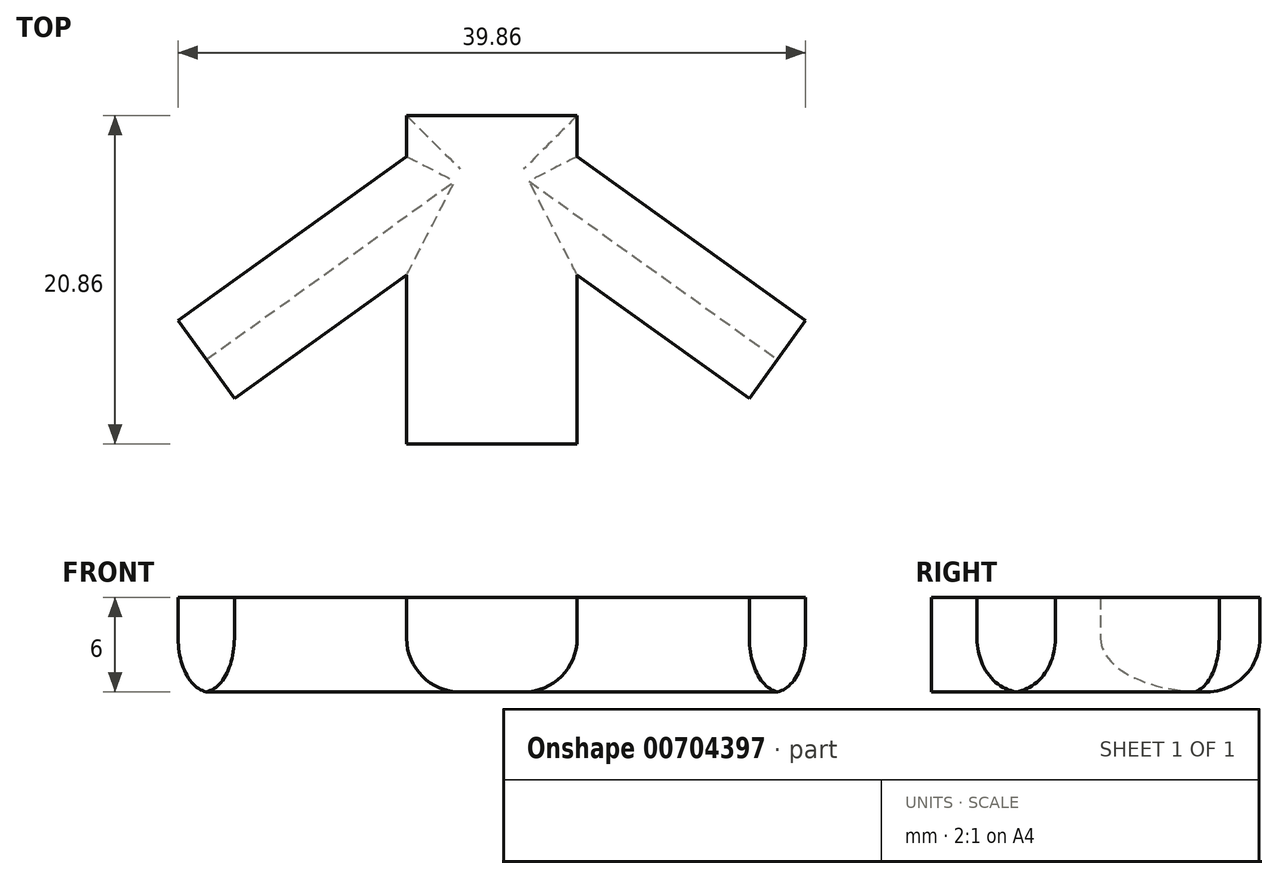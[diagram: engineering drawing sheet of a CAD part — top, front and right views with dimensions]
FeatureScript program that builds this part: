
annotation { "Feature Type Name" : "Feature", "Feature Type Description" : "" }
export const myFeature = defineFeature(function(context is Context, id is Id, definition is map)
    precondition{}
    {
        {
            var Q0;
            Q0=qCreatedBy(makeId("Top.planeOp"),FACE);
            var sketch = newSketch(context, id + "F0", { "sketchPlane" : qUnion([Q0])});
            skLineSegment(sketch, "E0", {"start": v(-5.41, 0) * mm, "end": v(-5.41, -10.73) * mm});
            skLineSegment(sketch, "E1", {"start": v(-5.41, -10.73) * mm, "end": v(0, -10.73) * mm});
            skLineSegment(sketch, "E2", {"start": v(-5.41, 0) * mm, "end": v(-16.36, -7.85) * mm});
            skLineSegment(sketch, "E3", {"start": v(-16.36, -7.85) * mm, "end": v(-19.93, -2.87) * mm});
            skLineSegment(sketch, "E4", {"start": v(-19.93, -2.87) * mm, "end": v(-5.41, 7.54) * mm});
            skLineSegment(sketch, "E5", {"start": v(-5.41, 7.54) * mm, "end": v(0, 7.54) * mm});
            skLineSegment(sketch, "E6.MirrorCS", {"start": v(5.41, -10.73) * mm, "end": v(0, -10.73) * mm});
            skLineSegment(sketch, "E7.MirrorCS", {"start": v(5.41, 0) * mm, "end": v(5.41, -10.73) * mm});
            skLineSegment(sketch, "E8.MirrorCS", {"start": v(5.41, 0) * mm, "end": v(16.36, -7.85) * mm});
            skLineSegment(sketch, "E9.MirrorCS", {"start": v(16.36, -7.85) * mm, "end": v(19.93, -2.87) * mm});
            skLineSegment(sketch, "E10.MirrorCS", {"start": v(19.93, -2.87) * mm, "end": v(5.41, 7.54) * mm});
            skLineSegment(sketch, "E11.MirrorCS", {"start": v(5.41, 7.54) * mm, "end": v(0, 7.54) * mm});
            skLineSegment(sketch, "E12", {"start": v(-5.41, 7.54) * mm, "end": v(-5.41, 10.13) * mm});
            skLineSegment(sketch, "E13", {"start": v(-5.41, 10.13) * mm, "end": v(0, 10.13) * mm});
            skLineSegment(sketch, "E14.MirrorCS", {"start": v(5.41, 10.13) * mm, "end": v(0, 10.13) * mm});
            skLineSegment(sketch, "E15.MirrorCS", {"start": v(5.41, 7.54) * mm, "end": v(5.41, 10.13) * mm});
            skLineSegment(sketch, "E16", {"start": v(-5.41, -6.95) * mm, "end": v(5.41, -6.95) * mm});
            skLineSegment(sketch, "E17", {"start": v(-5.41, -3.17) * mm, "end": v(5.41, -3.17) * mm});
            skLineSegment(sketch, "E18", {"start": v(-5.41, 0) * mm, "end": v(5.41, 0) * mm});
            skLineSegment(sketch, "E19", {"start": v(-15.92, 0) * mm, "end": v(-12.07, -5.37) * mm});
            skPoint(sketch, "E19.endSnap0", {"position": v(5.41, -5.37) * mm});
            skLineSegment(sketch, "E20", {"start": v(-12.67, 2.33) * mm, "end": v(-9.1, -2.64) * mm});
            skLineSegment(sketch, "E21", {"start": v(-8.72, 5.17) * mm, "end": v(-5.41, 0) * mm});
            skLineSegment(sketch, "E22", {"start": v(-5.41, 7.54) * mm, "end": v(-5.41, 0) * mm});
            skLineSegment(sketch, "E23.MirrorCS", {"start": v(5.41, 7.54) * mm, "end": v(5.41, 0) * mm});
            skLineSegment(sketch, "E24.MirrorCS", {"start": v(8.72, 5.17) * mm, "end": v(5.41, 0) * mm});
            skLineSegment(sketch, "E25.MirrorCS", {"start": v(12.67, 2.33) * mm, "end": v(9.1, -2.64) * mm});
            skLineSegment(sketch, "E26.MirrorCS", {"start": v(15.92, 0) * mm, "end": v(12.07, -5.37) * mm});
            skLineSegment(sketch, "E27", {"start": v(-5.41, 3.77) * mm, "end": v(5.41, 3.77) * mm});
            skSolve(sketch);
        }
        {
            var Q0;
            {var subQ0=sQuery(id+"F0.wireOp",EDGE,"E3");Q0=makeQuery(id+"F0.imprint","IMPRINT",FACE,{"disambiguationData":[TD([[makeQuery(id+"F0.imprint","IMPRINT",EDGE,{"derivedFrom":subQ0}),-1.0]])]});}
            var Q1;
            {var subQ0=sQuery(id+"F0.wireOp",EDGE,"E20");Q1=makeQuery(id+"F0.imprint","IMPRINT",FACE,{"disambiguationData":[TD([[makeQuery(id+"F0.imprint","IMPRINT",EDGE,{"derivedFrom":subQ0}),-1.0]])]});}
            var Q2;
            {var subQ2=sQuery(id+"F0.wireOp",EDGE,"E20");Q2=makeQuery(id+"F0.imprint","IMPRINT",FACE,{"disambiguationData":[TD([[makeQuery(id+"F0.imprint","IMPRINT",EDGE,{"derivedFrom":subQ2}),1.0]])]});}
            var Q3;
            {var subQ3=sQuery(id+"F0.wireOp",EDGE,"E21");Q3=makeQuery(id+"F0.imprint","IMPRINT",FACE,{"disambiguationData":[TD([[makeQuery(id+"F0.imprint","IMPRINT",EDGE,{"derivedFrom":subQ3}),1.0]])]});}
            var Q4;
            {var subQ4=sQuery(id+"F0.wireOp",EDGE,"E5");Q4=makeQuery(id+"F0.imprint","IMPRINT",FACE,{"disambiguationData":[TD([[makeQuery(id+"F0.imprint","IMPRINT",EDGE,{"derivedFrom":subQ4}),-1.0]])]});}
            var Q5;
            Q5=makeQuery(id+"F0.imprint","IMPRINT",FACE,{"disambiguationData":[TD([[makeQuery(id+"F0.imprint","IMPRINT",EDGE,{"derivedFrom":sQuery(id+"F0.wireOp",EDGE,"E5")}),1.0]])]});
            var Q6;
            {var subQ3=sQuery(id+"F0.wireOp",EDGE,"E24.MirrorCS");Q6=makeQuery(id+"F0.imprint","IMPRINT",FACE,{"disambiguationData":[TD([[makeQuery(id+"F0.imprint","IMPRINT",EDGE,{"derivedFrom":subQ3}),-1.0]])]});}
            var Q7;
            {var subQ0=sQuery(id+"F0.wireOp",EDGE,"E24.MirrorCS");Q7=makeQuery(id+"F0.imprint","IMPRINT",FACE,{"disambiguationData":[TD([[makeQuery(id+"F0.imprint","IMPRINT",EDGE,{"derivedFrom":subQ0}),1.0]])]});}
            var Q8;
            {var subQ0=sQuery(id+"F0.wireOp",EDGE,"E25.MirrorCS");Q8=makeQuery(id+"F0.imprint","IMPRINT",FACE,{"disambiguationData":[TD([[makeQuery(id+"F0.imprint","IMPRINT",EDGE,{"derivedFrom":subQ0}),1.0]])]});}
            var Q9;
            {var subQ0=sQuery(id+"F0.wireOp",EDGE,"E9.MirrorCS");Q9=makeQuery(id+"F0.imprint","IMPRINT",FACE,{"disambiguationData":[TD([[makeQuery(id+"F0.imprint","IMPRINT",EDGE,{"derivedFrom":subQ0}),1.0]])]});}
            var Q10;
            {var subQ0=sQuery(id+"F0.wireOp",EDGE,"E18");Q10=makeQuery(id+"F0.imprint","IMPRINT",FACE,{"disambiguationData":[TD([[makeQuery(id+"F0.imprint","IMPRINT",EDGE,{"derivedFrom":subQ0}),1.0]])]});}
            var Q11;
            {var subQ0=sQuery(id+"F0.wireOp",EDGE,"E16");Q11=makeQuery(id+"F0.imprint","IMPRINT",FACE,{"disambiguationData":[TD([[makeQuery(id+"F0.imprint","IMPRINT",EDGE,{"derivedFrom":subQ0}),1.0]])]});}
            var Q12;
            {var subQ2=sQuery(id+"F0.wireOp",EDGE,"E17");Q12=makeQuery(id+"F0.imprint","IMPRINT",FACE,{"disambiguationData":[TD([[makeQuery(id+"F0.imprint","IMPRINT",EDGE,{"derivedFrom":subQ2}),1.0]])]});}
            var Q13;
            {var subQ3=sQuery(id+"F0.wireOp",EDGE,"E1");Q13=makeQuery(id+"F0.imprint","IMPRINT",FACE,{"disambiguationData":[TD([[makeQuery(id+"F0.imprint","IMPRINT",EDGE,{"derivedFrom":subQ3}),1.0]])]});}
            extrude(context, id + "F1", {"entities" : qUnion([Q0, Q1, Q2, Q3, Q4, Q5, Q6, Q7, Q8, Q9, Q10, Q11, Q12, Q13]), "depth" : 6 * mm, "offsetDistance" : 25 * mm});
        }
        {
            var Q0;
            Q0=makeQuery(id+"F1.opExtrude","CAP_EDGE",EDGE,{"disambiguationData":[OSD([sQuery(id+"F0.wireOp",EDGE,"E10.MirrorCS")])],"isStart":true});
            var Q1;
            Q1=makeQuery(id+"F1.opExtrude","CAP_EDGE",EDGE,{"disambiguationData":[OSD([sQuery(id+"F0.wireOp",EDGE,"E8.MirrorCS")])],"isStart":true});
            var Q2;
            Q2=makeQuery(id+"F1.opExtrude","CAP_EDGE",EDGE,{"disambiguationData":[OSD([sQuery(id+"F0.wireOp",EDGE,"E7.MirrorCS")])],"isStart":true});
            var Q3;
            Q3=makeQuery(id+"F1.opExtrude","CAP_EDGE",EDGE,{"disambiguationData":[OSD([sQuery(id+"F0.wireOp",EDGE,"E0")])],"isStart":true});
            var Q4;
            Q4=makeQuery(id+"F1.opExtrude","CAP_EDGE",EDGE,{"disambiguationData":[OSD([sQuery(id+"F0.wireOp",EDGE,"E2")])],"isStart":true});
            var Q5;
            Q5=makeQuery(id+"F1.opExtrude","CAP_EDGE",EDGE,{"disambiguationData":[OSD([sQuery(id+"F0.wireOp",EDGE,"E4")])],"isStart":true});
            var Q6;
            Q6=makeQuery(id+"F1.opExtrude","CAP_EDGE",EDGE,{"disambiguationData":[OSD([sQuery(id+"F0.wireOp",EDGE,"E15.MirrorCS")])],"isStart":true});
            var Q7;
            Q7=makeQuery(id+"F1.opExtrude","CAP_EDGE",EDGE,{"disambiguationData":[OSD([sQuery(id+"F0.wireOp",EDGE,"E12")])],"isStart":true});
            var Q8;
            Q8=makeQuery(id+"F1.opExtrude","CAP_EDGE",EDGE,{"disambiguationData":[OSD([sQuery(id+"F0.wireOp",EDGE,"E13"),sQuery(id+"F0.wireOp",EDGE,"E14.MirrorCS")])],"isStart":true});
            fillet(context, id + "F2", {"entities" : qUnion([Q0, Q1, Q2, Q3, Q4, Q5, Q6, Q7, Q8]), "radius" : 3.4 * mm, "tangentPropagation" : true, "allowEdgeOverflow" : false});
        }
    });
